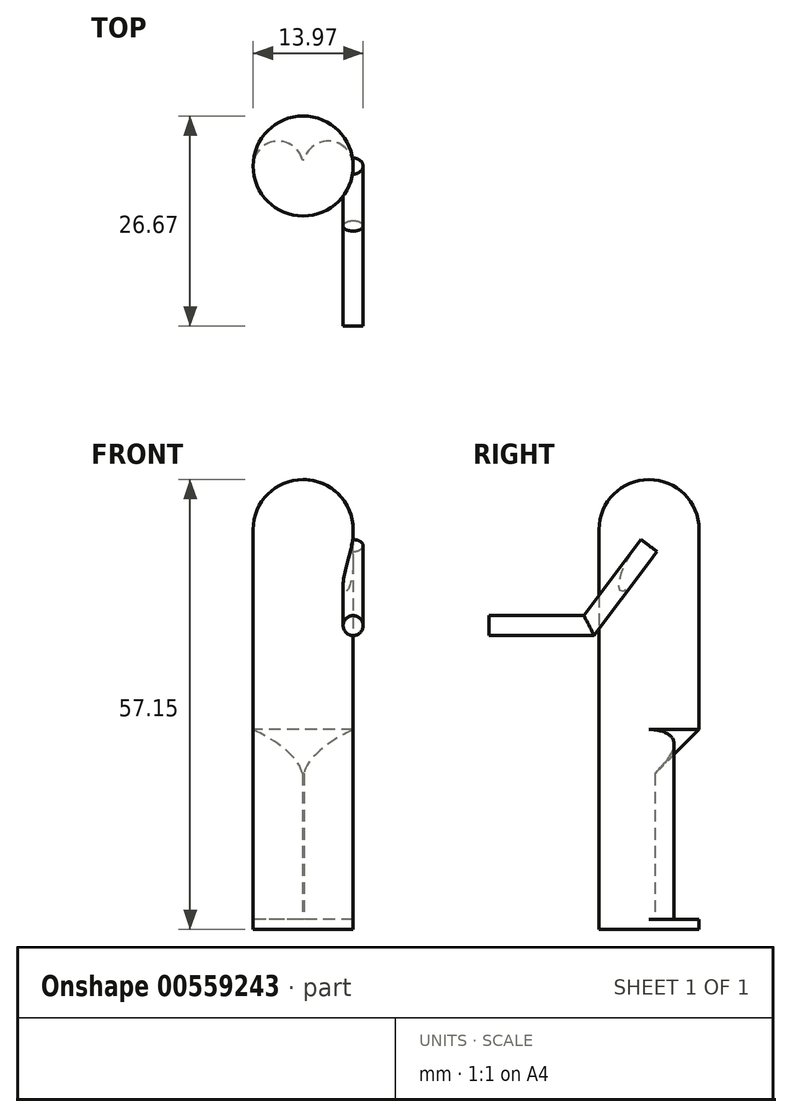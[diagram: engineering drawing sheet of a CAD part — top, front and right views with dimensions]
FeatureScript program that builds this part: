
annotation { "Feature Type Name" : "Feature", "Feature Type Description" : "" }
export const myFeature = defineFeature(function(context is Context, id is Id, definition is map)
    precondition{}
    {
        {
            var Q0;
            Q0=qCreatedBy(makeId("Top.planeOp"),FACE);
            var sketch = newSketch(context, id + "F0", { "sketchPlane" : qUnion([Q0])});
            skCircle(sketch, "E0", {"center": v(0, 0) * mm, "radius": 6.35 * mm});
            skArc(sketch, "E1", {"start": v(0.14, -0.92) * mm, "mid": v(6.35, 0.09) * mm, "end": v(0.09, 0.74) * mm});
            skArc(sketch, "E2.MirrorC", {"start": v(-0.14, -0.92) * mm, "mid": v(-6.35, 0.09) * mm, "end": v(-0.09, 0.74) * mm});
            skLineSegment(sketch, "E3", {"start": v(-0.14, -0.92) * mm, "end": v(0.14, -0.92) * mm});
            skLineSegment(sketch, "E4", {"start": v(0.09, 0.74) * mm, "end": v(-0.09, 0.74) * mm});
            skSolve(sketch);
        }
        {
            var Q0;
            {var subQ0=sQuery(id+"F0.wireOp",EDGE,"E2.MirrorC");var subQ1=makeQuery(id+"F0.imprint","INTERSECT",VERTEX,{"derivedFrom":[sQuery(id+"F0.wireOp",EDGE,"E0"),subQ0]});Q0=makeQuery(id+"F0.imprint","IMPRINT",FACE,{"disambiguationData":[TD([[makeQuery(id+"F0.imprint","IMPRINT",EDGE,{"disambiguationData":[TD([[subQ1,-1.0]])],"derivedFrom":subQ0}),-1.0]])]});}
            var Q1;
            {var subQ0=sQuery(id+"F0.wireOp",EDGE,"E1");var subQ1=makeQuery(id+"F0.imprint","INTERSECT",VERTEX,{"derivedFrom":[sQuery(id+"F0.wireOp",EDGE,"E0"),subQ0]});Q1=makeQuery(id+"F0.imprint","IMPRINT",FACE,{"disambiguationData":[TD([[makeQuery(id+"F0.imprint","IMPRINT",EDGE,{"disambiguationData":[TD([[subQ1,-1.0]])],"derivedFrom":subQ0}),1.0]])]});}
            extrude(context, id + "F1", {"entities" : qUnion([Q0, Q1]), "depth" : 25.4 * mm, "offsetDistance" : 25.4 * mm});
        }
        {
            var Q0;
            Q0=makeQuery(id+"F1.opExtrude","CAP_FACE",FACE,{"disambiguationData":[OSD([sQuery(id+"F0.wireOp",EDGE,"E2.MirrorC")])],"isStart":false});
            var sketch = newSketch(context, id + "F2", { "sketchPlane" : qUnion([Q0])});
            skCircle(sketch, "E5", {"center": v(0, 0) * mm, "radius": 6.35 * mm});
            skSolve(sketch);
        }
        {
            var Q0;
            Q0=makeQuery(id+"F2.imprint","IMPRINT",FACE,{"disambiguationData":[TD([[makeQuery(id+"F2.imprint","IMPRINT",EDGE,{"derivedFrom":sQuery(id+"F2.wireOp",EDGE,"E5")}),1.0]])]});
            var Q1;
            Q1=makeQuery(id+"F2.imprint","IMPRINT",FACE,{"disambiguationData":[TD([[makeQuery(id+"F2.imprint","IMPRINT",EDGE,{"derivedFrom":makeQuery(id+"F1.opExtrude","CAP_EDGE",EDGE,{"disambiguationData":[OSD([sQuery(id+"F0.wireOp",EDGE,"E2.MirrorC")])],"isStart":false})}),-1.0]])]});
            extrude(context, id + "F3", {"entities" : qUnion([Q0, Q1]), "operationType" : NewBodyOperationType.ADD, "depth" : 25.4 * mm, "offsetDistance" : 25.4 * mm, "hasSecondDirection" : true, "secondDirectionOppositeDirection" : true, "secondDirectionDepth" : 25.4 * mm, "hasSecondDirectionDraft" : true, "secondDirectionDraftAngle" : 45 * degree, "secondDirectionDraftPullDirection" : true});
        }
        {
            var Q0;
            Q0=qCreatedBy(makeId("Front.planeOp"),FACE);
            var sketch = newSketch(context, id + "F4", { "sketchPlane" : qUnion([Q0])});
            skLineSegment(sketch, "E6", {"start": v(0, 50.8) * mm, "end": v(0, 57.15) * mm});
            skArc(sketch, "E7", {"start": v(0, 57.15) * mm, "mid": v(-4.5, 55.3) * mm, "end": v(-6.35, 50.8) * mm});
            skLineSegment(sketch, "E8", {"start": v(0, 50.8) * mm, "end": v(-6.35, 50.8) * mm});
            skSolve(sketch);
        }
        {
            var Q0;
            Q0 = qSketchRegion(id + "F4", true);
            var Q1;
            Q1=sQuery(id+"F4.wireOp",EDGE,"E6");
            revolve(context, id + "F5", {"operationType" : NewBodyOperationType.ADD, "entities" : qUnion([Q0]), "axis" : qUnion([Q1]), "revolveType" : RevolveType.FULL});
        }
        {
            var Q0;
            Q0=qCreatedBy(makeId("Right.planeOp"),FACE);
            cPlane(context, id + "F6", {"entities" : qUnion([Q0]), "cplaneType" : CPlaneType.OFFSET, "offset" : 6.35 * mm, "width" : 152.4 * mm, "height" : 152.4 * mm});
        }
        {
            var Q0;
            Q0=qCreatedBy(id+"F6.planeOp",FACE);
            var sketch = newSketch(context, id + "F7", { "sketchPlane" : qUnion([Q0])});
            skLineSegment(sketch, "E9", {"start": v(0, 48.76) * mm, "end": v(-7.62, 38.6) * mm});
            skLineSegment(sketch, "E10", {"start": v(-7.62, 38.6) * mm, "end": v(-20.32, 38.6) * mm});
            skSolve(sketch);
        }
        {
            var Q0;
            Q0=qCreatedBy(makeId("Front.planeOp"),FACE);
            cPlane(context, id + "F8", {"entities" : qUnion([Q0]), "cplaneType" : CPlaneType.OFFSET, "offset" : 20.32 * mm, "width" : 152.4 * mm, "height" : 152.4 * mm});
        }
        {
            var Q0;
            Q0=qCreatedBy(id+"F8.planeOp",FACE);
            var sketch = newSketch(context, id + "F9", { "sketchPlane" : qUnion([Q0])});
            skCircle(sketch, "E11", {"center": v(6.35, 38.6) * mm, "radius": 1.27 * mm});
            skSolve(sketch);
        }
        {
            var Q0;
            Q0=makeQuery(id+"F9.imprint","IMPRINT",FACE,{"disambiguationData":[TD([[makeQuery(id+"F9.imprint","IMPRINT",EDGE,{"derivedFrom":sQuery(id+"F9.wireOp",EDGE,"E11")}),1.0]])]});
            var Q1;
            Q1 = qConstructionFilter(qBodyType(qCreatedBy(id + "F7" ,EDGE), BodyType.WIRE), ConstructionObject.NO);
            sweep(context, id + "F10", {"operationType" : NewBodyOperationType.ADD, "profiles" : qUnion([Q0]), "path" : qUnion([Q1])});
        }
        {
            var Q0;
            Q0 = qSketchRegion(id + "F0", true);
            extrude(context, id + "F11", {"entities" : qUnion([Q0]), "operationType" : NewBodyOperationType.ADD, "depth" : 1.27 * mm, "offsetDistance" : 25.4 * mm});
        }
    });
